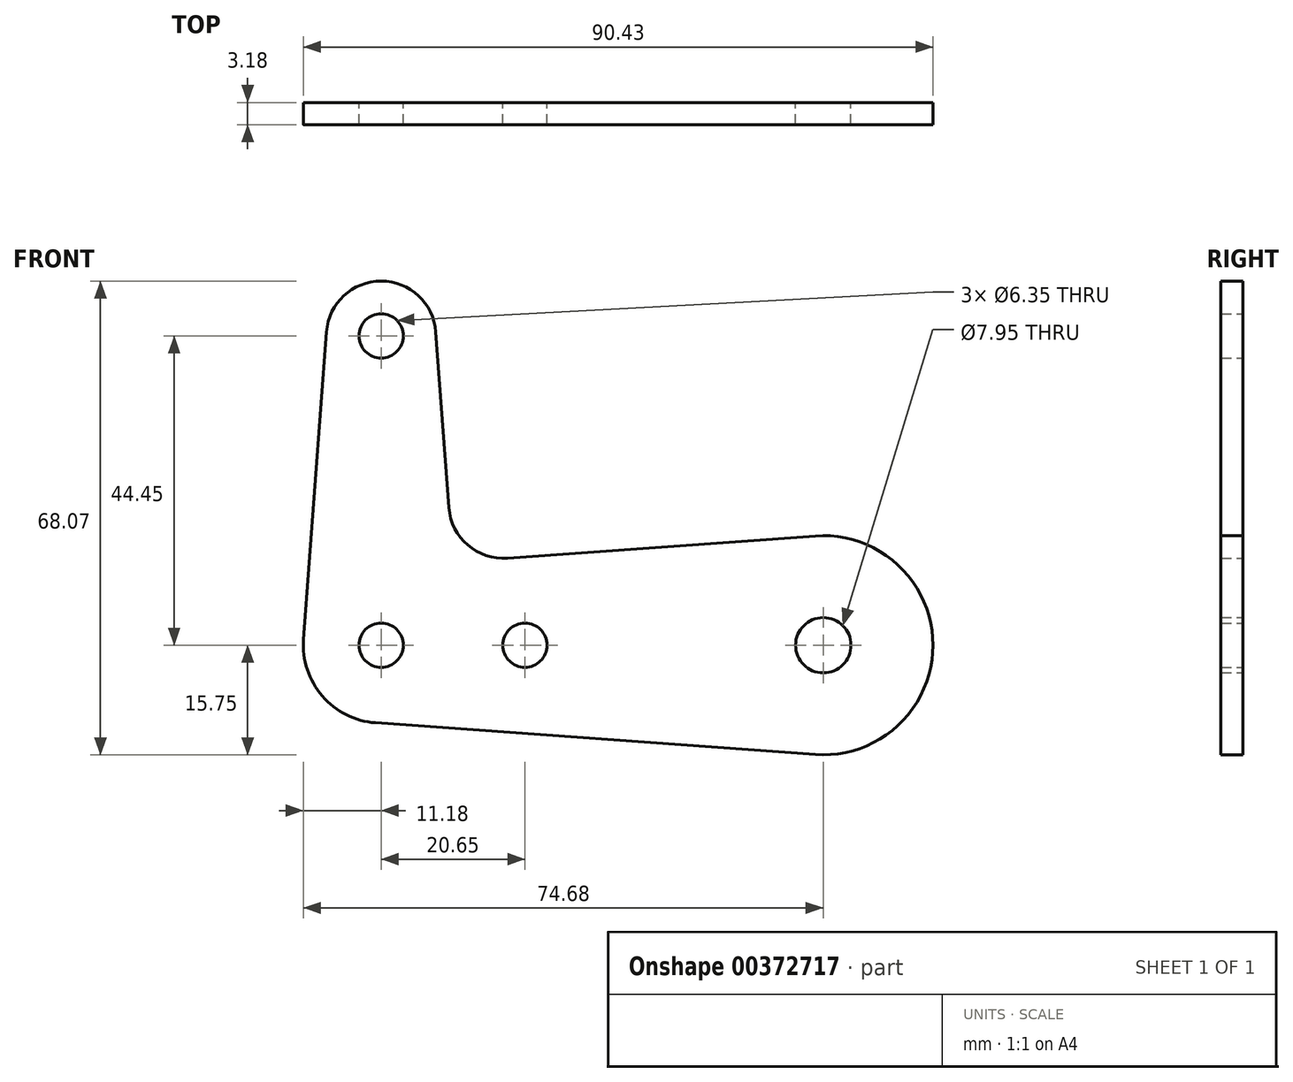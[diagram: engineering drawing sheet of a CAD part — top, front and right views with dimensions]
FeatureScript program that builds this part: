
annotation { "Feature Type Name" : "Feature", "Feature Type Description" : "" }
export const myFeature = defineFeature(function(context is Context, id is Id, definition is map)
    precondition{}
    {
        {
            var Q0;
            Q0=qCreatedBy(makeId("Front.planeOp"),FACE);
            var sketch = newSketch(context, id + "F0", { "sketchPlane" : qUnion([Q0])});
            skCircle(sketch, "E0", {"center": v(0, 0) * mm, "radius": 3.18 * mm});
            skCircle(sketch, "E1", {"center": v(42.85, 0) * mm, "radius": 3.98 * mm});
            skCircle(sketch, "E2", {"center": v(-20.65, 0) * mm, "radius": 3.18 * mm});
            skCircle(sketch, "E3", {"center": v(-20.65, 44.45) * mm, "radius": 3.18 * mm});
            skArc(sketch, "E4", {"start": v(-31.8, 0.83) * mm, "mid": v(-29.1, -7.3) * mm, "end": v(-21.45, -11.15) * mm});
            skArc(sketch, "E5", {"start": v(-12.8, 45.03) * mm, "mid": v(-20.65, 52.32) * mm, "end": v(-28.5, 45.03) * mm});
            skArc(sketch, "E6", {"start": v(41.72, -15.7) * mm, "mid": v(58.6, 0) * mm, "end": v(41.72, 15.7) * mm});
            skLineSegment(sketch, "E7", {"start": v(-28.5, 45.03) * mm, "end": v(-31.8, 0.83) * mm});
            skLineSegment(sketch, "E8", {"start": v(-21.45, -11.15) * mm, "end": v(41.72, -15.7) * mm});
            skLineSegment(sketch, "E9", {"start": v(-12.8, 45.03) * mm, "end": v(-10.92, 19.78) * mm});
            skLineSegment(sketch, "E10", {"start": v(-2.5, 12.52) * mm, "end": v(41.72, 15.7) * mm});
            skPoint(sketch, "E11.visualSharp", {"position": v(-10.33, 11.95) * mm});
            skArc(sketch, "E11.filletArc", {"start": v(-10.92, 19.78) * mm, "mid": v(-8.21, 14.4) * mm, "end": v(-2.5, 12.52) * mm});
            skSolve(sketch);
        }
        {
            var Q0;
            Q0 = qSketchRegion(id + "F0", true);
            extrude(context, id + "F1", {"entities" : qUnion([Q0]), "endBound" : BoundingType.SYMMETRIC, "depth" : 3.17 * mm});
        }
    });
